# Revit family: Furniture_Chairs_Stolab_Pinnockio
name_source: partatom
category: Furniture
revit_build: Autodesk Revit 2018 (Build: 20190510_1515(x64)
units: mm (PartAtom-declared; Revit-internal decimal feet)

## family parameters
Always vertical = Yes
Cut with Voids When Loaded = No
OmniClass Number = 23.40.20.14.14.11
OmniClass Title = Chairs
Room Calculation Point = No
Shared = No
Work Plane-Based = No

## types (1)
- Pinnockio chair
    AssetType = Movable
    BIMObjectName = Furniture_Chairs_Stolab_Pinnockio
    Brand = Stolab
    Category = Chairs
    Color = Various
    Cost = 0 $
    Description = It's always exciting to go back and look in a leading designer's furniture archive. At Stolab, we have long admired Yngve Ekström's beautiful pin chair Pinnockio. A chair that was in our range during the 50s and 60s. When Stolab turned 110, it felt like a good opportunity to once again highlight this neat wicker chair as a tribute to one of the greats in Swedish furniture design from us at the "wicker chair factory" in Smålandsstenar. Pinnockio is made of solid birch and has stable legs that are screwed into the seat. The neat impression is enhanced by the seven back pins that taper together in the solid top piece. A stick chair that, due to its design language, fits many types of tables.
    Designer = Yngve Ekström
    ExpectedLife = Years
    IfcExportAs = IfcFurnishingElementType
    IfcExportType = CHAIR
    MainColor = Various
    Manufacturer = Stolab
    ManufacturerName = Stolab
    ManufacturerURL = https://www.stolab.se
    Material = Wood
    Model = Pinnockio chair
    ModelNumber = 9990580157
    NBSDescription = Domestic chairs
    NBSReference = 45-35-20/365
    Name = Pinnockio
    NominalDepth = 470 mm
    NominalHeight = 840 mm
    NominalLength = 450 mm  [stored 1.47638 ft]
    ProductInformation = It's always exciting to go back and look in a leading designer's furniture archive. At Stolab, we have long admired Yngve Ekström's beautiful pin chair Pinnockio. A chair that was in our range during the 50s and 60s. When Stolab turned 110, it felt like a good opportunity to once again highlight this neat wicker chair as a tribute to one of the greats in Swedish furniture design from us at the "wicker chair factory" in Smålandsstenar. Pinnockio is made of solid birch and has stable legs that are screwed into the seat. The neat impression is enhanced by the seven back pins that taper together in the solid top piece. A stick chair that, due to its design language, fits many types of tables.
    SeatingHeight = 450 mm  [stored 1.47638 ft]
    Shape = Sculptured
    Size = 450x470x840 mm
    URL = http://www.stolab.se
    Uniclass2 = Pr_40_50_12_48
    Uniclass2015Description = Dining chairs
    Uniclass2015Reference = Pr_40_50_12_22
    Version = 1
    VersionDate = 12/11/2021
    WarrantyDurationUnit = Years

note: [stored X ft] marks values corroborated as IEEE doubles in the binary element streams (Revit-internal decimal feet)

## geometry (parser evidence)
native form markers: Sweep x8
no freeform markers — native parametric forms only
